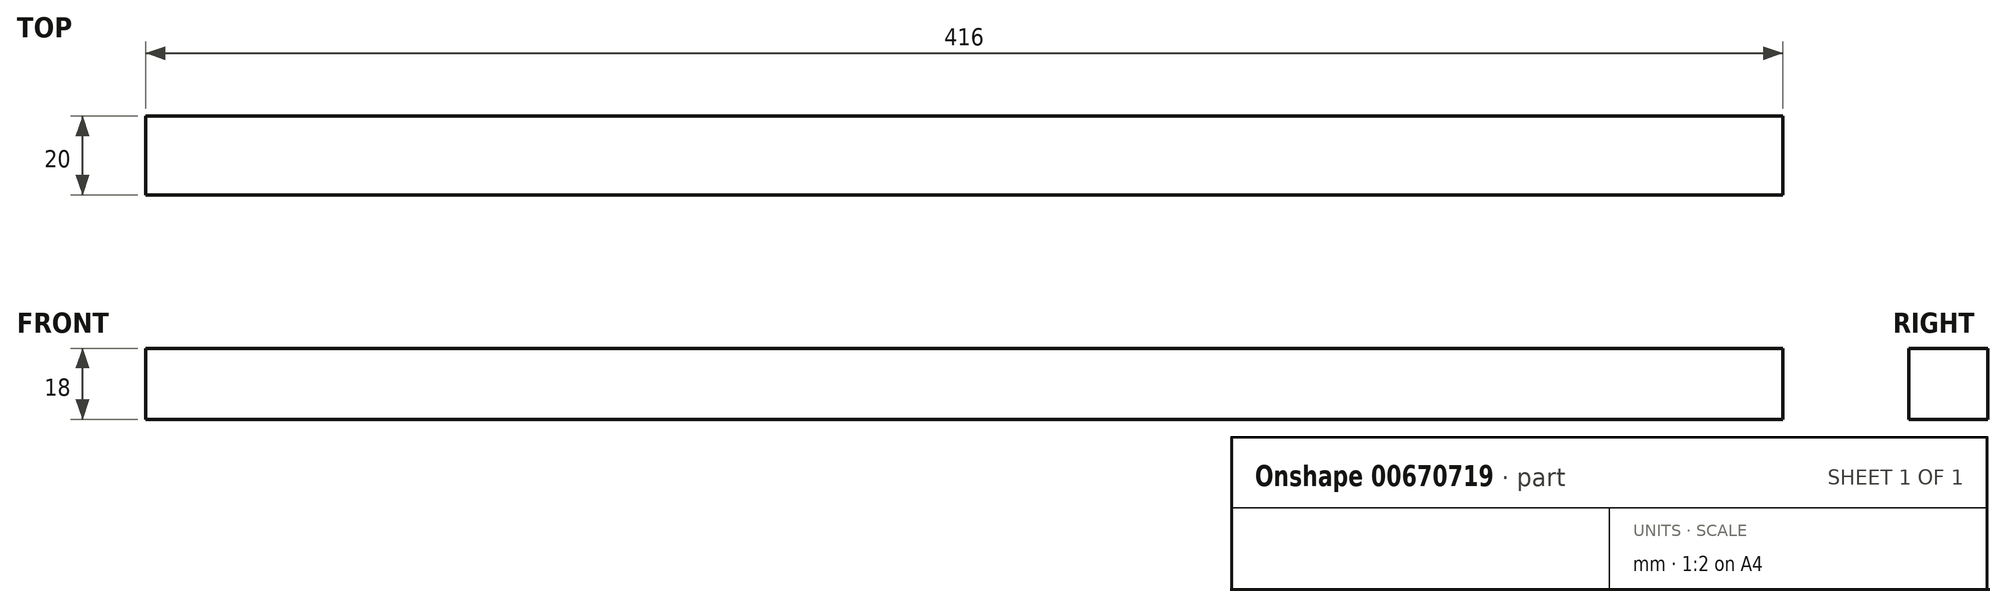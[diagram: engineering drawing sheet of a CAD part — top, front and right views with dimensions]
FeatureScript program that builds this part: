
annotation { "Feature Type Name" : "Feature", "Feature Type Description" : "" }
export const myFeature = defineFeature(function(context is Context, id is Id, definition is map)
    precondition{}
    {
        {
            var Q0;
            Q0=qCreatedBy(makeId("Top.planeOp"),FACE);
            var sketch = newSketch(context, id + "F0", { "sketchPlane" : qUnion([Q0])});
            skLineSegment(sketch, "E0.bottom", {"start": v(208, 10) * mm, "end": v(-208, 10) * mm});
            skLineSegment(sketch, "E0.top", {"start": v(208, -10) * mm, "end": v(-208, -10) * mm});
            skLineSegment(sketch, "E0.left", {"start": v(208, 10) * mm, "end": v(208, -10) * mm});
            skLineSegment(sketch, "E0.right", {"start": v(-208, 10) * mm, "end": v(-208, -10) * mm});
            skPoint(sketch, "E0.middle", {"position": v(0, 0) * mm});
            skSolve(sketch);
        }
        {
            var Q0;
            Q0 = qSketchRegion(id + "F0", true);
            extrude(context, id + "F1", {"entities" : qUnion([Q0]), "endBound" : BoundingType.SYMMETRIC, "depth" : 18 * mm, "offsetDistance" : 25 * mm});
        }
    });
